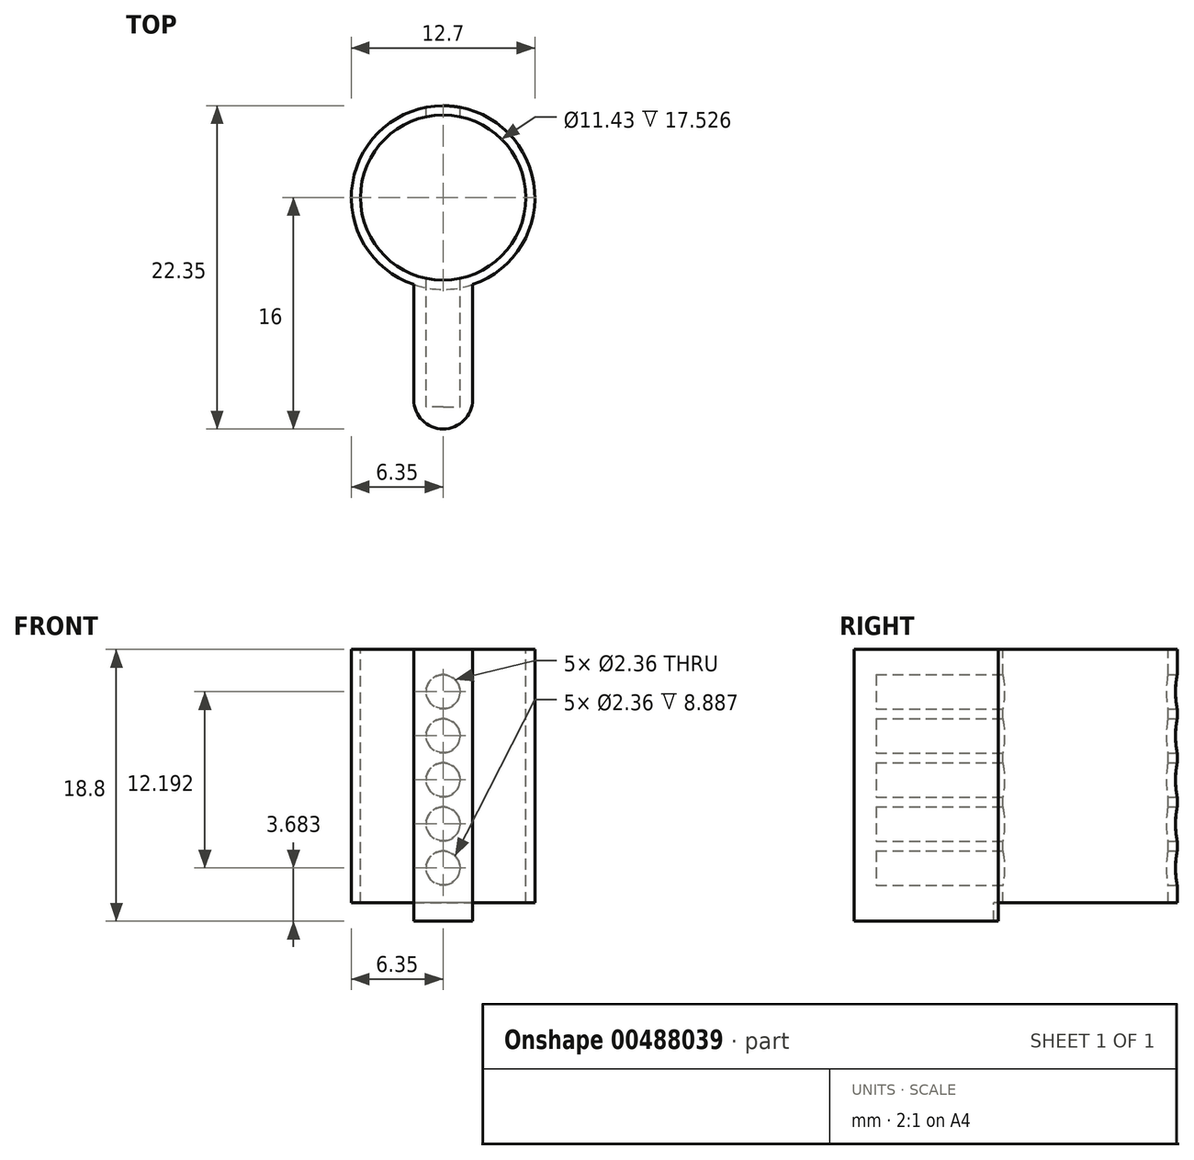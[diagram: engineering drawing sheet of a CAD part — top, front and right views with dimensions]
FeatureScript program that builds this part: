
annotation { "Feature Type Name" : "Feature", "Feature Type Description" : "" }
export const myFeature = defineFeature(function(context is Context, id is Id, definition is map)
    precondition{}
    {
        {
            var Q0;
            Q0=qCreatedBy(makeId("Top.planeOp"),FACE);
            var sketch = newSketch(context, id + "F0", { "sketchPlane" : qUnion([Q0])});
            skCircle(sketch, "E0", {"center": v(0, 0) * mm, "radius": 6.35 * mm});
            skArc(sketch, "E1", {"start": v(-2.03, -13.97) * mm, "mid": v(0, -16) * mm, "end": v(2.03, -13.97) * mm});
            skLineSegment(sketch, "E2.left", {"start": v(-2.03, -13.97) * mm, "end": v(-2.03, -6.02) * mm});
            skLineSegment(sketch, "E2.right", {"start": v(2.03, -13.97) * mm, "end": v(2.03, -6.02) * mm});
            skSolve(sketch);
        }
        {
            var Q0;
            Q0 = qSketchRegion(id + "F0", true);
            extrude(context, id + "F1", {"entities" : qUnion([Q0]), "depth" : 17.53 * mm, "offsetDistance" : 25.4 * mm});
        }
        {
            var Q0;
            Q0=makeQuery(id+"F0.imprint","IMPRINT",FACE,{"disambiguationData":[TD([[makeQuery(id+"F0.imprint","IMPRINT",EDGE,{"derivedFrom":sQuery(id+"F0.wireOp",EDGE,"E1")}),1.0]])]});
            extrude(context, id + "F2", {"entities" : qUnion([Q0]), "operationType" : NewBodyOperationType.ADD, "oppositeDirection" : true, "depth" : 1.27 * mm, "offsetDistance" : 25.4 * mm});
        }
        {
            var Q0;
            Q0=makeQuery(id+"F1.opExtrude","CAP_FACE",FACE,{"disambiguationData":[OSD([sQuery(id+"F0.wireOp",EDGE,"E0"),sQuery(id+"F0.wireOp",EDGE,"E1"),sQuery(id+"F0.wireOp",EDGE,"E2.left"),sQuery(id+"F0.wireOp",EDGE,"E2.right")])],"isStart":false});
            var sketch = newSketch(context, id + "F3", { "sketchPlane" : qUnion([Q0])});
            skCircle(sketch, "E3", {"center": v(0, 0) * mm, "radius": 5.72 * mm});
            skSolve(sketch);
        }
        {
            var Q0;
            Q0 = qSketchRegion(id + "F3", true);
            var Q1;
            Q1=makeQuery(id+"F1.opExtrude","CAP_FACE",FACE,{"disambiguationData":[OSD([sQuery(id+"F0.wireOp",EDGE,"E0"),sQuery(id+"F0.wireOp",EDGE,"E1"),sQuery(id+"F0.wireOp",EDGE,"E2.left"),sQuery(id+"F0.wireOp",EDGE,"E2.right")])],"isStart":true});
            extrude(context, id + "F4", {"entities" : qUnion([Q0]), "operationType" : NewBodyOperationType.REMOVE, "endBound" : BoundingType.UP_TO_SURFACE, "oppositeDirection" : true, "depth" : 25.4 * mm, "endBoundEntityFace" : qUnion([Q1]), "offsetDistance" : 25.4 * mm});
        }
        {
            var Q0;
            Q0=qCreatedBy(makeId("Front.planeOp"),FACE);
            cPlane(context, id + "F5", {"entities" : qUnion([Q0]), "cplaneType" : CPlaneType.OFFSET, "offset" : 6.35 * mm, "oppositeDirection" : true, "width" : 152.4 * mm, "height" : 152.4 * mm});
        }
        {
            var Q0;
            Q0=qCreatedBy(id+"F5.planeOp",FACE);
            var sketch = newSketch(context, id + "F6", { "sketchPlane" : qUnion([Q0])});
            skCircle(sketch, "E4", {"center": v(0, 2.41) * mm, "radius": 1.18 * mm});
            skCircle(sketch, "E5", {"center": v(0, 5.46) * mm, "radius": 1.18 * mm});
            skCircle(sketch, "E6", {"center": v(0, 8.5) * mm, "radius": 1.18 * mm});
            skCircle(sketch, "E7", {"center": v(0, 11.56) * mm, "radius": 1.18 * mm});
            skCircle(sketch, "E8", {"center": v(0, 14.6) * mm, "radius": 1.18 * mm});
            skSolve(sketch);
        }
        {
            var Q0;
            Q0 = qSketchRegion(id + "F6", true);
            extrude(context, id + "F7", {"entities" : qUnion([Q0]), "operationType" : NewBodyOperationType.REMOVE, "depth" : 20.83 * mm, "offsetDistance" : 25.4 * mm});
        }
    });
